# Revit family: Sarlam_Eclairage_Hublot_Chartres_Infini_T2_Anti_Vandale_Diam_435mm_3000Lm
name_source: partatom
category: Luminaires
units: mm (PartAtom-declared; Revit-internal decimal feet)

## family parameters
Cote de connecteur circulaire = Utiliser le diamètre
Couper avec des vides une fois chargée = Non
Hôte = Face
Partagée = Non
Point de calcul de pièce = Non
Source d'éclairage = Oui
Type d'élément = Normal

## types (8) — shared parameters
Adapté à un montage au plafond = Oui
Adapté à un montage en applique = Oui
Adapté à un montage en saillie = Oui
Adapté à un montage encastré = Non
Adapté à une suspension = Non
Angle de l'inclinaison = 0.00°
Angle du faisceau = Faisceau libre
Antivandale Formes 2-4-7 = Oui
Appareillage = Appareil à LED commandé en courant
Classe de protection = II
Condition Générale d'Utilisation = https://export.legrand.com
Diamètre externe = 435 mm  [stored 1.42717 ft]
Douille = Sans
Elévation par défaut = 2500 mm  [stored 8.2021 ft]
Emettre la visibilité des formes dans le rendu = Non
Emettre à partir du diamètre du cercle = 300 mm
Fabricant = LEGRAND
Fichier de distribution photométrique = SL532009.ies
Filtre de couleur = 16777215
Flux lumineux utile lm = 3000
Gradation des changements de température de couleur de lampe = <Aucun>
Hauteur/profondeur = 90 mm  [stored 0.295276 ft]
Indice de rendu des couleurs CRI = 80-89
Largeur = 435 mm  [stored 1.42717 ft]
Largeur d'encastrement = 435 mm  [stored 1.42717 ft]
Longueur = 435 mm  [stored 1.42717 ft]
Matériau du boîtier/corps = Plastique
Puissance de la lampe en Multiwatt = 21/39W
Répartition lumineuse = Symétrique
Source lumineuse = Led non interchangeable
Température de couleur K MAX = 4000
Température de couleur K MIN = 4000
Tension nominale (Un) V MAX = 253
Tension nominale (Un) V MIN = 207
Type de tension = CA
URL = http://www.legrandoc.com
zero-valued in all types: Courant nominal mA MAX, Courant nominal mA MIN, Diamètre d'encastrement, Hauteur/profondeur d'encastrement, Longueur d'encastrement, Puissance du système W

## per-type parameters (varying)
| type | Avec détecteur crépusculaire | Avec détecteur de mouvement | Couleur du boîtier/corps | Description | Indice de protection (IP) | Indice de protection contre les chocs (IK) | Modèle | Type de variation | Zone de détection |
| ON/OFF BLANC | Non | Non | LEGRAND - Blanc | CHARTRES INFINI 3000LM 4000K AV ON/OFF BLANC | IP55 | IK10 | SL-532015 | Non régulable |  |
| ON/OFF ANTHRACITE | Non | Non | LEGRAND - Anthracite | CHARTRES INFINI 3000LM 4000K AV ON/OFF ANTHRACITE | IP55 | IK10 | SL-532016 | Non régulable |  |
| ON/OFF GRIS METAL | Non | Non | LEGRAND - Gris métal | CHARTRES INFINI 3000LM 4000K AV ON/OFF GRIS METAL | IP55 | IK10 | SL-532017 | Non régulable |  |
| Détection BLANC | Oui | Oui | LEGRAND - Blanc | CHARTRES INFINI 3000LM 4000K  AV DETECTION HF BLANC | IP55 | IK10 | SL-532055 | Autre | Détection à 2,5m haut Plafond: Ø6m maxi Mur: Ellipse 16*17m |
| Détection ANTHRACITE | Oui | Oui | LEGRAND - Anthracite | CHARTRES INFINI 3000LM 4000K  AV DETECTION HF ANTHRACITE | IP55 | IK10 | SL-532056 | Autre | Détection à 2,5m haut Plafond: Ø6m maxi Mur: Ellipse 16*17m |
| Détection GRIS METAL | Oui | Oui | LEGRAND - Gris métal | CHARTRES INFINI 3000LM 4000K  AV DETECTION HF GRIS METAL | IP55 | IK10 | SL-532057 | Autre | Détection à 2,5m haut Plafond: Ø6m maxi Mur: Ellipse 16*17m |
| Renforcé-ON/OFF | Non | Non | LEGRAND - Blanc | CHARTRES INFINI 3000LM 4000K SOLIROC ON/OFF BLANC | IP66 | >IK10 | SL-532098 | Non régulable |  |
| Renforcé-Détection | Oui | Oui | LEGRAND - Blanc | CHARTRES INFINI 3000LM 4000K  SOLIROC DETECTION HF BLANC | IP66 | >IK10 | SL-532099 | Autre | Détection à 2,5m haut Plafond: Ø6m maxi Mur: Ellipse 16*17m |

note: [stored X ft] marks values corroborated as IEEE doubles in the binary element streams (Revit-internal decimal feet)

## geometry (parser evidence)
native form markers: Blend x10
no freeform markers — native parametric forms only
